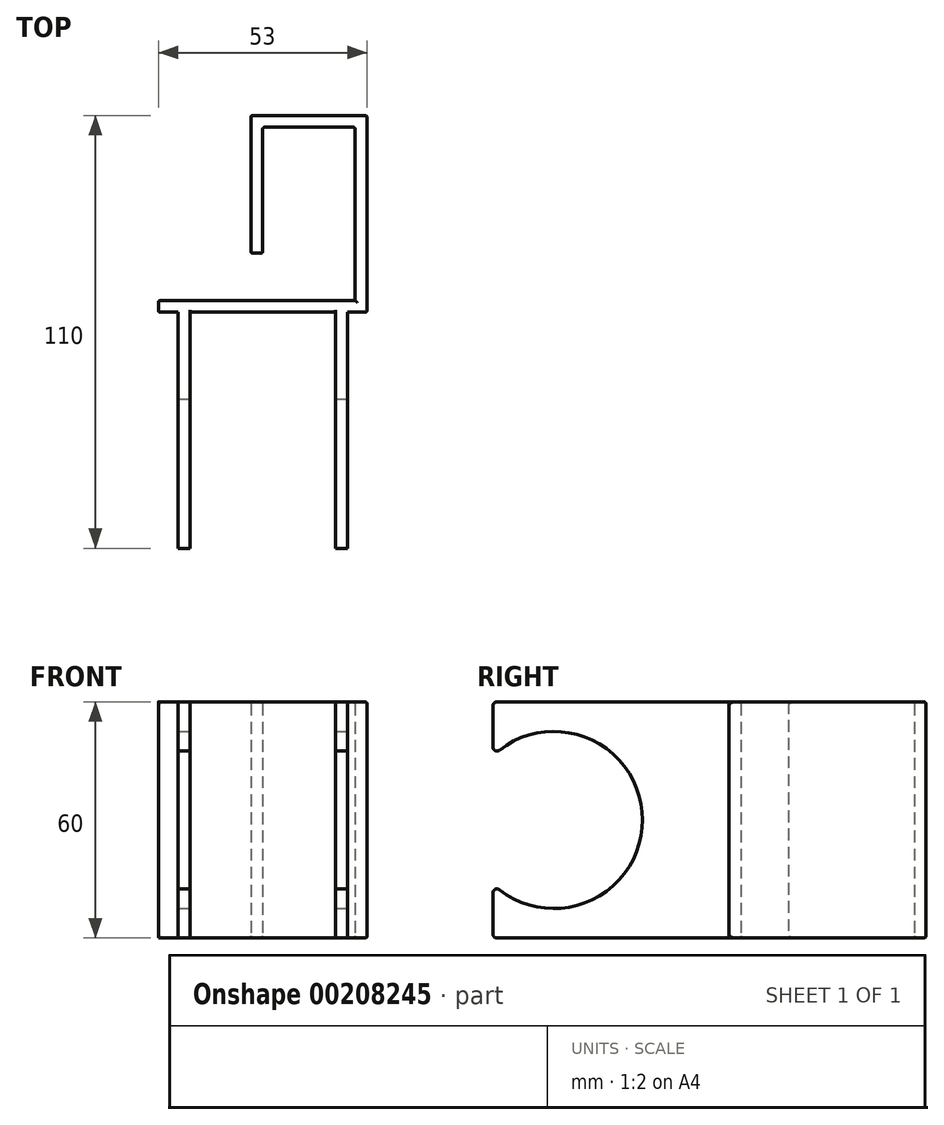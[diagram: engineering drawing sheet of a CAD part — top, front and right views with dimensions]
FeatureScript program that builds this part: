
annotation { "Feature Type Name" : "Feature", "Feature Type Description" : "" }
export const myFeature = defineFeature(function(context is Context, id is Id, definition is map)
    precondition{}
    {
        {
            var Q0;
            Q0=qCreatedBy(makeId("Top.planeOp"),FACE);
            var sketch = newSketch(context, id + "F0", { "sketchPlane" : qUnion([Q0])});
            skLineSegment(sketch, "E0.bottom", {"start": v(0, 0) * mm, "end": v(-3, 0) * mm});
            skLineSegment(sketch, "E0.top", {"start": v(0, -50) * mm, "end": v(-3, -50) * mm});
            skLineSegment(sketch, "E0.left", {"start": v(0, 0) * mm, "end": v(0, -50) * mm});
            skLineSegment(sketch, "E0.right", {"start": v(-3, -3) * mm, "end": v(-3, -47) * mm});
            skLineSegment(sketch, "E1.bottom", {"start": v(-3, -50) * mm, "end": v(-5, -50) * mm});
            skLineSegment(sketch, "E1.top", {"start": v(-3, -47) * mm, "end": v(-53, -47) * mm});
            skLineSegment(sketch, "E1.right", {"start": v(-53, -50) * mm, "end": v(-53, -47) * mm});
            skLineSegment(sketch, "E2.bottom", {"start": v(-3, 0) * mm, "end": v(-29.5, 0) * mm});
            skLineSegment(sketch, "E2.top", {"start": v(-3, -3) * mm, "end": v(-26.5, -3) * mm});
            skLineSegment(sketch, "E2.right", {"start": v(-29.5, 0) * mm, "end": v(-29.5, -3) * mm});
            skLineSegment(sketch, "E3.top", {"start": v(-29.5, -35) * mm, "end": v(-26.5, -35) * mm});
            skLineSegment(sketch, "E3.left", {"start": v(-29.5, -3) * mm, "end": v(-29.5, -35) * mm});
            skLineSegment(sketch, "E3.right", {"start": v(-26.5, -3) * mm, "end": v(-26.5, -35) * mm});
            skLineSegment(sketch, "E4", {"start": v(-53, -50) * mm, "end": v(-48, -50) * mm});
            skLineSegment(sketch, "E5", {"start": v(0, -50) * mm, "end": v(-5, -50) * mm});
            skLineSegment(sketch, "E6.top", {"start": v(-48, -110) * mm, "end": v(-45, -110) * mm});
            skLineSegment(sketch, "E6.left", {"start": v(-48, -50) * mm, "end": v(-48, -110) * mm});
            skLineSegment(sketch, "E6.right", {"start": v(-45, -50) * mm, "end": v(-45, -110) * mm});
            skLineSegment(sketch, "E7.top", {"start": v(-5, -110) * mm, "end": v(-8, -110) * mm});
            skLineSegment(sketch, "E7.left", {"start": v(-5, -50) * mm, "end": v(-5, -110) * mm});
            skLineSegment(sketch, "E7.right", {"start": v(-8, -50) * mm, "end": v(-8, -110) * mm});
            skLineSegment(sketch, "E8.trimOffspring", {"start": v(-48, -50) * mm, "end": v(-53, -50) * mm});
            skLineSegment(sketch, "E9.trimOffspring", {"start": v(-8, -50) * mm, "end": v(-45, -50) * mm});
            skSolve(sketch);
        }
        {
            var Q0;
            Q0 = qSketchRegion(id + "F0", true);
            extrude(context, id + "F1", {"entities" : qUnion([Q0]), "depth" : 60 * mm});
        }
        {
            var Q0;
            Q0=qCreatedBy(makeId("Right.planeOp"),FACE);
            var sketch = newSketch(context, id + "F2", { "sketchPlane" : qUnion([Q0])});
            skLineSegment(sketch, "E10", {"start": v(-110, 0) * mm, "end": v(-50, 0) * mm});
            skLineSegment(sketch, "E11", {"start": v(-110, 60) * mm, "end": v(-50, 60) * mm});
            skLineSegment(sketch, "E12", {"start": v(-50, 60) * mm, "end": v(-50, 0) * mm});
            skCircle(sketch, "E13", {"center": v(-94.54, 30) * mm, "radius": 22.5 * mm});
            skSolve(sketch);
        }
        {
            var Q0;
            Q0=makeQuery(id+"F2.imprint","IMPRINT",FACE,{"disambiguationData":[TD([[makeQuery(id+"F2.imprint","IMPRINT",EDGE,{"derivedFrom":sQuery(id+"F2.wireOp",EDGE,"E13")}),1.0]])]});
            extrude(context, id + "F3", {"entities" : qUnion([Q0]), "operationType" : NewBodyOperationType.REMOVE, "oppositeDirection" : true, "depth" : 50 * mm});
        }
        {
            var Q0;
            Q0=makeQuery(id+"F3.boolean.opBoolean","INTERSECT",EDGE,{"disambiguationData":[OD(1.0)],"derivedFrom":[makeQuery(id+"F1.opExtrude","SWEPT_FACE",FACE,{"disambiguationData":[OSD([sQuery(id+"F0.wireOp",EDGE,"E7.top")])]}),makeQuery(id+"F3.opExtrude","SWEPT_FACE",FACE,{"disambiguationData":[OSD([sQuery(id+"F2.wireOp",EDGE,"E13")])]})]});
            var Q1;
            Q1=makeQuery(id+"F3.boolean.opBoolean","INTERSECT",EDGE,{"disambiguationData":[OD(1.0)],"derivedFrom":[makeQuery(id+"F1.opExtrude","SWEPT_FACE",FACE,{"disambiguationData":[OSD([sQuery(id+"F0.wireOp",EDGE,"E6.top")])]}),makeQuery(id+"F3.opExtrude","SWEPT_FACE",FACE,{"disambiguationData":[OSD([sQuery(id+"F2.wireOp",EDGE,"E13")])]})]});
            var Q2;
            Q2=makeQuery(id+"F3.boolean.opBoolean","INTERSECT",EDGE,{"disambiguationData":[OD(0.0)],"derivedFrom":[makeQuery(id+"F1.opExtrude","SWEPT_FACE",FACE,{"disambiguationData":[OSD([sQuery(id+"F0.wireOp",EDGE,"E7.top")])]}),makeQuery(id+"F3.opExtrude","SWEPT_FACE",FACE,{"disambiguationData":[OSD([sQuery(id+"F2.wireOp",EDGE,"E13")])]})]});
            var Q3;
            Q3=makeQuery(id+"F3.boolean.opBoolean","INTERSECT",EDGE,{"disambiguationData":[OD(0.0)],"derivedFrom":[makeQuery(id+"F1.opExtrude","SWEPT_FACE",FACE,{"disambiguationData":[OSD([sQuery(id+"F0.wireOp",EDGE,"E6.top")])]}),makeQuery(id+"F3.opExtrude","SWEPT_FACE",FACE,{"disambiguationData":[OSD([sQuery(id+"F2.wireOp",EDGE,"E13")])]})]});
            var Q4;
            Q4=makeQuery(id+"F1.opExtrude","CAP_EDGE",EDGE,{"disambiguationData":[OSD([sQuery(id+"F0.wireOp",EDGE,"E7.top")])],"isStart":false});
            var Q5;
            Q5=makeQuery(id+"F1.opExtrude","CAP_EDGE",EDGE,{"disambiguationData":[OSD([sQuery(id+"F0.wireOp",EDGE,"E6.top")])],"isStart":false});
            var Q6;
            Q6=makeQuery(id+"F1.opExtrude","CAP_EDGE",EDGE,{"disambiguationData":[OSD([sQuery(id+"F0.wireOp",EDGE,"E7.top")])],"isStart":true});
            var Q7;
            Q7=makeQuery(id+"F1.opExtrude","CAP_EDGE",EDGE,{"disambiguationData":[OSD([sQuery(id+"F0.wireOp",EDGE,"E6.top")])],"isStart":true});
            fillet(context, id + "F4", {"entities" : qUnion([Q0, Q1, Q2, Q3, Q4, Q5, Q6, Q7]), "radius" : 1 * mm, "tangentPropagation" : true, "allowEdgeOverflow" : false});
        }
        {
            var Q0;
            Q0=makeQuery(id+"F1.opExtrude","SWEPT_EDGE",EDGE,{"disambiguationData":[OSD([sQuery(id+"F0.wireOp",EDGE,"E3.top"),sQuery(id+"F0.wireOp",EDGE,"E3.left")])]});
            var Q1;
            Q1=makeQuery(id+"F1.opExtrude","SWEPT_EDGE",EDGE,{"disambiguationData":[OSD([sQuery(id+"F0.wireOp",EDGE,"E3.top"),sQuery(id+"F0.wireOp",EDGE,"E3.right")])]});
            var Q2;
            Q2=makeQuery(id+"F1.opExtrude","CAP_EDGE",EDGE,{"disambiguationData":[OSD([sQuery(id+"F0.wireOp",EDGE,"E3.right")])],"isStart":false});
            var Q3;
            Q3=makeQuery(id+"F1.opExtrude","CAP_EDGE",EDGE,{"disambiguationData":[OSD([sQuery(id+"F0.wireOp",EDGE,"E2.right"),sQuery(id+"F0.wireOp",EDGE,"E3.left")])],"isStart":false});
            var Q4;
            Q4=makeQuery(id+"F1.opExtrude","CAP_EDGE",EDGE,{"disambiguationData":[OSD([sQuery(id+"F0.wireOp",EDGE,"E2.right"),sQuery(id+"F0.wireOp",EDGE,"E3.left")])],"isStart":true});
            var Q5;
            Q5=makeQuery(id+"F1.opExtrude","CAP_EDGE",EDGE,{"disambiguationData":[OSD([sQuery(id+"F0.wireOp",EDGE,"E3.right")])],"isStart":true});
            var Q6;
            Q6=makeQuery(id+"F1.opExtrude","SWEPT_EDGE",EDGE,{"disambiguationData":[OSD([sQuery(id+"F0.wireOp",EDGE,"E2.bottom"),sQuery(id+"F0.wireOp",EDGE,"E2.right")])]});
            var Q7;
            Q7=makeQuery(id+"F1.opExtrude","CAP_EDGE",EDGE,{"disambiguationData":[OSD([sQuery(id+"F0.wireOp",EDGE,"E2.top")])],"isStart":true});
            var Q8;
            Q8=makeQuery(id+"F1.opExtrude","CAP_EDGE",EDGE,{"disambiguationData":[OSD([sQuery(id+"F0.wireOp",EDGE,"E0.bottom"),sQuery(id+"F0.wireOp",EDGE,"E2.bottom")])],"isStart":true});
            var Q9;
            Q9=makeQuery(id+"F1.opExtrude","CAP_EDGE",EDGE,{"disambiguationData":[OSD([sQuery(id+"F0.wireOp",EDGE,"E2.top")])],"isStart":false});
            var Q10;
            Q10=makeQuery(id+"F1.opExtrude","CAP_EDGE",EDGE,{"disambiguationData":[OSD([sQuery(id+"F0.wireOp",EDGE,"E0.bottom"),sQuery(id+"F0.wireOp",EDGE,"E2.bottom")])],"isStart":false});
            var Q11;
            Q11=makeQuery(id+"F1.opExtrude","SWEPT_EDGE",EDGE,{"disambiguationData":[OSD([sQuery(id+"F0.wireOp",EDGE,"E0.bottom"),sQuery(id+"F0.wireOp",EDGE,"E0.left")])]});
            var Q12;
            Q12=makeQuery(id+"F1.opExtrude","SWEPT_EDGE",EDGE,{"disambiguationData":[OSD([sQuery(id+"F0.wireOp",EDGE,"E2.top"),sQuery(id+"F0.wireOp",EDGE,"E3.right")])]});
            var Q13;
            Q13=makeQuery(id+"F1.opExtrude","SWEPT_EDGE",EDGE,{"disambiguationData":[OSD([sQuery(id+"F0.wireOp",EDGE,"E0.right"),sQuery(id+"F0.wireOp",EDGE,"E2.top")])]});
            var Q14;
            Q14=makeQuery(id+"F1.opExtrude","CAP_EDGE",EDGE,{"disambiguationData":[OSD([sQuery(id+"F0.wireOp",EDGE,"E0.right")])],"isStart":false});
            var Q15;
            Q15=makeQuery(id+"F1.opExtrude","CAP_EDGE",EDGE,{"disambiguationData":[OSD([sQuery(id+"F0.wireOp",EDGE,"E0.left")])],"isStart":false});
            var Q16;
            Q16=makeQuery(id+"F1.opExtrude","CAP_EDGE",EDGE,{"disambiguationData":[OSD([sQuery(id+"F0.wireOp",EDGE,"E0.right")])],"isStart":true});
            var Q17;
            Q17=makeQuery(id+"F1.opExtrude","CAP_EDGE",EDGE,{"disambiguationData":[OSD([sQuery(id+"F0.wireOp",EDGE,"E0.left")])],"isStart":true});
            var Q18;
            Q18=makeQuery(id+"F1.opExtrude","CAP_EDGE",EDGE,{"disambiguationData":[OSD([sQuery(id+"F0.wireOp",EDGE,"E1.top")])],"isStart":false});
            var Q19;
            Q19=makeQuery(id+"F1.opExtrude","CAP_EDGE",EDGE,{"disambiguationData":[OSD([sQuery(id+"F0.wireOp",EDGE,"E9.trimOffspring")])],"isStart":false});
            var Q20;
            Q20=makeQuery(id+"F1.opExtrude","CAP_EDGE",EDGE,{"disambiguationData":[OSD([sQuery(id+"F0.wireOp",EDGE,"E8.trimOffspring")])],"isStart":false});
            var Q21;
            Q21=makeQuery(id+"F1.opExtrude","CAP_EDGE",EDGE,{"disambiguationData":[OSD([sQuery(id+"F0.wireOp",EDGE,"E5")])],"isStart":false});
            var Q22;
            Q22=makeQuery(id+"F1.opExtrude","SWEPT_EDGE",EDGE,{"disambiguationData":[OSD([sQuery(id+"F0.wireOp",EDGE,"E0.left"),sQuery(id+"F0.wireOp",EDGE,"E5")])]});
            var Q23;
            Q23=makeQuery(id+"F1.opExtrude","CAP_EDGE",EDGE,{"disambiguationData":[OSD([sQuery(id+"F0.wireOp",EDGE,"E5")])],"isStart":true});
            var Q24;
            Q24=makeQuery(id+"F1.opExtrude","CAP_EDGE",EDGE,{"disambiguationData":[OSD([sQuery(id+"F0.wireOp",EDGE,"E1.top")])],"isStart":true});
            var Q25;
            Q25=makeQuery(id+"F1.opExtrude","CAP_EDGE",EDGE,{"disambiguationData":[OSD([sQuery(id+"F0.wireOp",EDGE,"E9.trimOffspring")])],"isStart":true});
            var Q26;
            Q26=makeQuery(id+"F1.opExtrude","CAP_EDGE",EDGE,{"disambiguationData":[OSD([sQuery(id+"F0.wireOp",EDGE,"E8.trimOffspring")])],"isStart":true});
            var Q27;
            Q27=makeQuery(id+"F1.opExtrude","SWEPT_EDGE",EDGE,{"disambiguationData":[OSD([sQuery(id+"F0.wireOp",EDGE,"E1.top"),sQuery(id+"F0.wireOp",EDGE,"E1.right")])]});
            var Q28;
            Q28=makeQuery(id+"F1.opExtrude","SWEPT_EDGE",EDGE,{"disambiguationData":[OSD([sQuery(id+"F0.wireOp",EDGE,"E1.right"),sQuery(id+"F0.wireOp",EDGE,"E8.trimOffspring")])]});
            fillet(context, id + "F5", {"entities" : qUnion([Q0, Q1, Q2, Q3, Q4, Q5, Q6, Q7, Q8, Q9, Q10, Q11, Q12, Q13, Q14, Q15, Q16, Q17, Q18, Q19, Q20, Q21, Q22, Q23, Q24, Q25, Q26, Q27, Q28]), "radius" : 0.5 * mm, "tangentPropagation" : true, "allowEdgeOverflow" : false});
        }
    });
